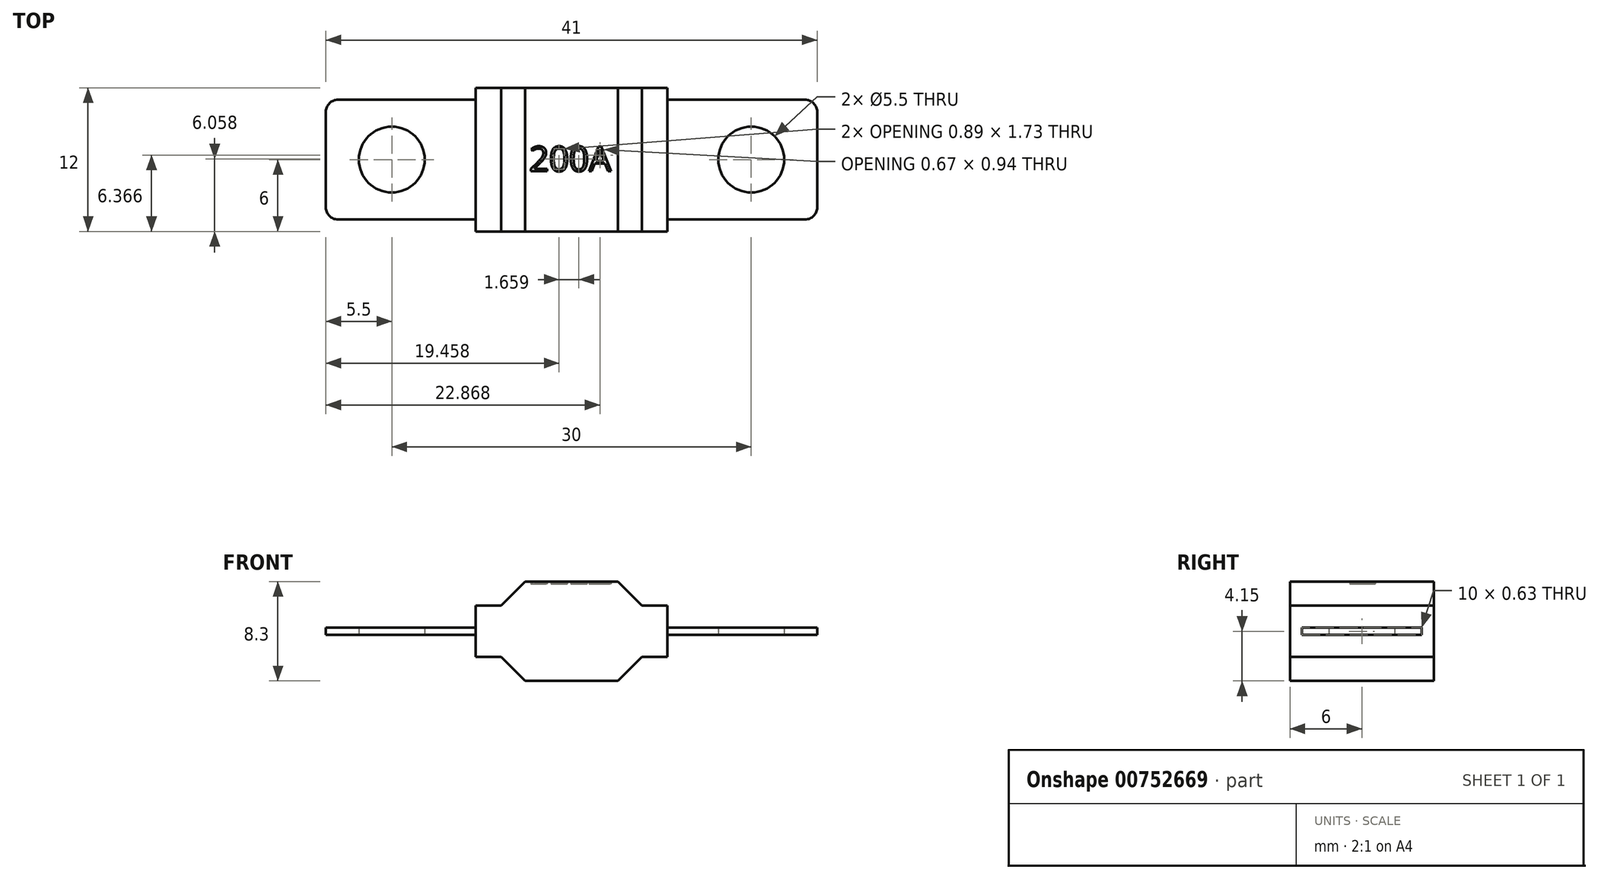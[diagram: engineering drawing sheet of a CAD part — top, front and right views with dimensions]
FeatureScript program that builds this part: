
annotation { "Feature Type Name" : "Feature", "Feature Type Description" : "" }
export const myFeature = defineFeature(function(context is Context, id is Id, definition is map)
    precondition{}
    {
        {
            var Q0;
            Q0=qCreatedBy(makeId("Top.planeOp"),FACE);
            var sketch = newSketch(context, id + "F0", { "sketchPlane" : qUnion([Q0])});
            skLineSegment(sketch, "E0.bottom", {"start": v(19.5, -5) * mm, "end": v(8, -5) * mm});
            skLineSegment(sketch, "E0.top", {"start": v(19.5, 5) * mm, "end": v(8, 5) * mm});
            skLineSegment(sketch, "E0.left", {"start": v(20.5, -4) * mm, "end": v(20.5, 4) * mm});
            skLineSegment(sketch, "E0.right", {"start": v(-20.5, -4) * mm, "end": v(-20.5, 4) * mm});
            skPoint(sketch, "E0.middle", {"position": v(0, 0) * mm});
            skLineSegment(sketch, "E1.bottom", {"start": v(8, -6) * mm, "end": v(-8, -6) * mm});
            skLineSegment(sketch, "E1.top", {"start": v(8, 6) * mm, "end": v(-8, 6) * mm});
            skLineSegment(sketch, "E1.left", {"start": v(8, -6) * mm, "end": v(8, 6) * mm});
            skLineSegment(sketch, "E1.right", {"start": v(-8, -6) * mm, "end": v(-8, 6) * mm});
            skCircle(sketch, "E2", {"center": v(-15, 0) * mm, "radius": 2.75 * mm});
            skPoint(sketch, "E2.centerSnap0", {"position": v(-20.5, 0) * mm});
            skCircle(sketch, "E3", {"center": v(15, 0) * mm, "radius": 2.75 * mm});
            skPoint(sketch, "E3.centerSnap0", {"position": v(20.5, 0) * mm});
            skLineSegment(sketch, "E4.bottom", {"start": v(15, -13.28) * mm, "end": v(-15, -13.28) * mm, "construction": true});
            skLineSegment(sketch, "E4.top", {"start": v(15, 13.28) * mm, "end": v(-15, 13.28) * mm, "construction": true});
            skLineSegment(sketch, "E4.left", {"start": v(15, -13.28) * mm, "end": v(15, 13.28) * mm, "construction": true});
            skLineSegment(sketch, "E4.right", {"start": v(-15, -13.28) * mm, "end": v(-15, 13.28) * mm, "construction": true});
            skLineSegment(sketch, "E5.trimOffspring", {"start": v(-8, 5) * mm, "end": v(-19.5, 5) * mm});
            skLineSegment(sketch, "E6.trimOffspring", {"start": v(-8, -5) * mm, "end": v(-19.5, -5) * mm});
            skPoint(sketch, "E7.visualSharp", {"position": v(-20.5, 5) * mm});
            skArc(sketch, "E7.filletArc", {"start": v(-19.5, 5) * mm, "mid": v(-20.2, 4.7) * mm, "end": v(-20.5, 4) * mm});
            skPoint(sketch, "E8.visualSharp", {"position": v(-20.5, -5) * mm});
            skArc(sketch, "E8.filletArc", {"start": v(-20.5, -4) * mm, "mid": v(-20.2, -4.7) * mm, "end": v(-19.5, -5) * mm});
            skPoint(sketch, "E9.visualSharp", {"position": v(20.5, -5) * mm});
            skArc(sketch, "E9.filletArc", {"start": v(19.5, -5) * mm, "mid": v(20.2, -4.7) * mm, "end": v(20.5, -4) * mm});
            skPoint(sketch, "E10.visualSharp", {"position": v(20.5, 5) * mm});
            skArc(sketch, "E10.filletArc", {"start": v(20.5, 4) * mm, "mid": v(20.2, 4.7) * mm, "end": v(19.5, 5) * mm});
            skSolve(sketch);
        }
        {
            var Q0;
            Q0=qSketchRegion(id+"F0",true);
            extrude(context, id + "F1", {"entities" : qUnion([Q0]), "depth" : 25 * mm, "offsetDistance" : 25 * mm});
        }
        {
            var Q0;
            Q0=makeQuery(id+"F1.opExtrude","SWEPT_FACE",FACE,{"disambiguationData":[OSD([sQuery(id+"F0.wireOp",EDGE,"E1.bottom")])]});
            var sketch = newSketch(context, id + "F2", { "sketchPlane" : qUnion([Q0])});
            skLineSegment(sketch, "E11", {"start": v(0, 25) * mm, "end": v(0, 0) * mm, "construction": true});
            skLineSegment(sketch, "E12.bottom", {"start": v(20.5, 12.19) * mm, "end": v(8, 12.19) * mm});
            skLineSegment(sketch, "E12.top", {"start": v(20.5, 12.82) * mm, "end": v(8, 12.82) * mm});
            skPoint(sketch, "E12.middle", {"position": v(0, 12.5) * mm});
            skLineSegment(sketch, "E13.bottom", {"start": v(8, 10.35) * mm, "end": v(5.86, 10.35) * mm});
            skLineSegment(sketch, "E13.top", {"start": v(8, 14.65) * mm, "end": v(5.86, 14.65) * mm});
            skLineSegment(sketch, "E13.left", {"start": v(8, 10.35) * mm, "end": v(8, 12.19) * mm});
            skLineSegment(sketch, "E13.right", {"start": v(-8, 10.35) * mm, "end": v(-8, 12.19) * mm});
            skLineSegment(sketch, "E14.bottom", {"start": v(3.86, 8.35) * mm, "end": v(-3.86, 8.35) * mm});
            skLineSegment(sketch, "E14.top", {"start": v(3.86, 16.65) * mm, "end": v(-3.86, 16.65) * mm});
            skLineSegment(sketch, "E15", {"start": v(3.86, 16.65) * mm, "end": v(5.86, 14.65) * mm});
            skLineSegment(sketch, "E16", {"start": v(-3.86, 16.65) * mm, "end": v(-5.86, 14.65) * mm});
            skLineSegment(sketch, "E17", {"start": v(-3.86, 8.35) * mm, "end": v(-5.86, 10.35) * mm});
            skLineSegment(sketch, "E18", {"start": v(3.86, 8.35) * mm, "end": v(5.86, 10.35) * mm});
            skLineSegment(sketch, "E19.trimOffspring", {"start": v(-5.86, 14.65) * mm, "end": v(-8, 14.65) * mm});
            skLineSegment(sketch, "E20.trimOffspring", {"start": v(-5.86, 10.35) * mm, "end": v(-8, 10.35) * mm});
            skLineSegment(sketch, "E21.trimOffspring", {"start": v(-8, 12.19) * mm, "end": v(-20.5, 12.19) * mm});
            skLineSegment(sketch, "E22.trimOffspring", {"start": v(-8, 12.81) * mm, "end": v(-20.5, 12.81) * mm});
            skLineSegment(sketch, "E23.trimOffspring", {"start": v(8, 12.82) * mm, "end": v(8, 14.65) * mm});
            skLineSegment(sketch, "E24.trimOffspring", {"start": v(-8, 12.81) * mm, "end": v(-8, 14.65) * mm});
            skLineSegment(sketch, "E25.bottom", {"start": v(20.85, -2.6) * mm, "end": v(-20.85, -2.6) * mm});
            skLineSegment(sketch, "E25.top", {"start": v(20.85, 27.6) * mm, "end": v(-20.85, 27.6) * mm});
            skLineSegment(sketch, "E25.left", {"start": v(20.85, -2.6) * mm, "end": v(20.85, 27.6) * mm});
            skLineSegment(sketch, "E25.right", {"start": v(-20.85, -2.6) * mm, "end": v(-20.85, 27.6) * mm});
            skPoint(sketch, "E12.left.end.orphan", {"position": v(21.22, 12.82) * mm});
            skPoint(sketch, "E26.orphan", {"position": v(21.22, 12.19) * mm});
            skPoint(sketch, "E27.orphan", {"position": v(-21.22, 12.81) * mm});
            skPoint(sketch, "E28.orphan", {"position": v(-21.22, 12.19) * mm});
            skLineSegment(sketch, "E29", {"start": v(20.5, 12.82) * mm, "end": v(20.5, 12.19) * mm});
            skLineSegment(sketch, "E30", {"start": v(-20.5, 12.81) * mm, "end": v(-20.5, 12.19) * mm});
            skSolve(sketch);
        }
        {
            var Q0;
            Q0=qSketchRegion(id+"F2",true);
            extrude(context, id + "F3", {"entities" : qUnion([Q0]), "operationType" : NewBodyOperationType.REMOVE, "oppositeDirection" : true, "depth" : 25 * mm, "offsetDistance" : 25 * mm});
        }
        {
            var Q0;
            Q0=makeQuery(id+"F3.boolean.opBoolean","COPY",FACE,{"derivedFrom":makeQuery(id+"F3.opExtrude","SWEPT_FACE",FACE,{"disambiguationData":[OSD([sQuery(id+"F2.wireOp",EDGE,"E14.top")])]})});
            var sketch = newSketch(context, id + "F4", { "sketchPlane" : qUnion([Q0])});
            skText(sketch, "E31", { "text": "200A", "fontName": "OpenSans-Regular.ttf"});
            const initialGuessF4  = {"E31": [-0.00353, -0.00098, 1, 0, 0.00209]};
            skSetInitialGuess(sketch, initialGuessF4);
            skSolve(sketch);
        }
        {
            var Q0;
            Q0=qSketchRegion(id+"F4",true);
            extrude(context, id + "F5", {"entities" : qUnion([Q0]), "operationType" : NewBodyOperationType.REMOVE, "oppositeDirection" : true, "depth" : .2 * mm, "offsetDistance" : 25 * mm});
        }
        {
            var Q0;
            Q0=makeQuery(id+"F5.boolean.opBoolean","COPY",FACE,{"derivedFrom":makeQuery(id+"F5.opExtrude","CAP_FACE",FACE,{"disambiguationData":[OSD([sQuery(id+"F4.wireOp",EDGE,"E31.sketch_text.stroke-0"),sQuery(id+"F4.wireOp",EDGE,"E31.sketch_text.stroke-1"),sQuery(id+"F4.wireOp",EDGE,"E31.sketch_text.stroke-2"),sQuery(id+"F4.wireOp",EDGE,"E31.sketch_text.stroke-3"),sQuery(id+"F4.wireOp",EDGE,"E31.sketch_text.stroke-4"),sQuery(id+"F4.wireOp",EDGE,"E31.sketch_text.stroke-5"),sQuery(id+"F4.wireOp",EDGE,"E31.sketch_text.stroke-6"),sQuery(id+"F4.wireOp",EDGE,"E31.sketch_text.stroke-7"),sQuery(id+"F4.wireOp",EDGE,"E31.sketch_text.stroke-8"),sQuery(id+"F4.wireOp",EDGE,"E31.sketch_text.stroke-9"),sQuery(id+"F4.wireOp",EDGE,"E31.sketch_text.stroke-10"),sQuery(id+"F4.wireOp",EDGE,"E31.sketch_text.stroke-11"),sQuery(id+"F4.wireOp",EDGE,"E31.sketch_text.stroke-12"),sQuery(id+"F4.wireOp",EDGE,"E31.sketch_text.stroke-13"),sQuery(id+"F4.wireOp",EDGE,"E31.sketch_text.stroke-14"),sQuery(id+"F4.wireOp",EDGE,"E31.sketch_text.stroke-15"),sQuery(id+"F4.wireOp",EDGE,"E31.sketch_text.stroke-16"),sQuery(id+"F4.wireOp",EDGE,"E31.sketch_text.stroke-17"),sQuery(id+"F4.wireOp",EDGE,"E31.sketch_text.stroke-18"),sQuery(id+"F4.wireOp",EDGE,"E31.sketch_text.stroke-19")])],"isStart":false})});
            var Q1;
            Q1=makeQuery(id+"F5.boolean.opBoolean","COPY",FACE,{"derivedFrom":makeQuery(id+"F5.opExtrude","CAP_FACE",FACE,{"disambiguationData":[OSD([sQuery(id+"F4.wireOp",EDGE,"E31.sketch_text.stroke-20"),sQuery(id+"F4.wireOp",EDGE,"E31.sketch_text.stroke-21"),sQuery(id+"F4.wireOp",EDGE,"E31.sketch_text.stroke-22"),sQuery(id+"F4.wireOp",EDGE,"E31.sketch_text.stroke-23"),sQuery(id+"F4.wireOp",EDGE,"E31.sketch_text.stroke-24"),sQuery(id+"F4.wireOp",EDGE,"E31.sketch_text.stroke-25"),sQuery(id+"F4.wireOp",EDGE,"E31.sketch_text.stroke-26"),sQuery(id+"F4.wireOp",EDGE,"E31.sketch_text.stroke-27"),sQuery(id+"F4.wireOp",EDGE,"E31.sketch_text.stroke-28"),sQuery(id+"F4.wireOp",EDGE,"E31.sketch_text.stroke-29"),sQuery(id+"F4.wireOp",EDGE,"E31.sketch_text.stroke-30"),sQuery(id+"F4.wireOp",EDGE,"E31.sketch_text.stroke-31"),sQuery(id+"F4.wireOp",EDGE,"E31.sketch_text.stroke-32"),sQuery(id+"F4.wireOp",EDGE,"E31.sketch_text.stroke-33"),sQuery(id+"F4.wireOp",EDGE,"E31.sketch_text.stroke-34"),sQuery(id+"F4.wireOp",EDGE,"E31.sketch_text.stroke-35")])],"isStart":false})});
            var Q2;
            Q2=makeQuery(id+"F5.boolean.opBoolean","COPY",FACE,{"derivedFrom":makeQuery(id+"F5.opExtrude","CAP_FACE",FACE,{"disambiguationData":[OSD([sQuery(id+"F4.wireOp",EDGE,"E31.sketch_text.stroke-36"),sQuery(id+"F4.wireOp",EDGE,"E31.sketch_text.stroke-37"),sQuery(id+"F4.wireOp",EDGE,"E31.sketch_text.stroke-38"),sQuery(id+"F4.wireOp",EDGE,"E31.sketch_text.stroke-39"),sQuery(id+"F4.wireOp",EDGE,"E31.sketch_text.stroke-40"),sQuery(id+"F4.wireOp",EDGE,"E31.sketch_text.stroke-41"),sQuery(id+"F4.wireOp",EDGE,"E31.sketch_text.stroke-42"),sQuery(id+"F4.wireOp",EDGE,"E31.sketch_text.stroke-43"),sQuery(id+"F4.wireOp",EDGE,"E31.sketch_text.stroke-44"),sQuery(id+"F4.wireOp",EDGE,"E31.sketch_text.stroke-45"),sQuery(id+"F4.wireOp",EDGE,"E31.sketch_text.stroke-46"),sQuery(id+"F4.wireOp",EDGE,"E31.sketch_text.stroke-47"),sQuery(id+"F4.wireOp",EDGE,"E31.sketch_text.stroke-48"),sQuery(id+"F4.wireOp",EDGE,"E31.sketch_text.stroke-49"),sQuery(id+"F4.wireOp",EDGE,"E31.sketch_text.stroke-50"),sQuery(id+"F4.wireOp",EDGE,"E31.sketch_text.stroke-51")])],"isStart":false})});
            var Q3;
            Q3=makeQuery(id+"F5.boolean.opBoolean","COPY",FACE,{"derivedFrom":makeQuery(id+"F5.opExtrude","CAP_FACE",FACE,{"disambiguationData":[OSD([sQuery(id+"F4.wireOp",EDGE,"E31.sketch_text.stroke-52"),sQuery(id+"F4.wireOp",EDGE,"E31.sketch_text.stroke-53"),sQuery(id+"F4.wireOp",EDGE,"E31.sketch_text.stroke-54"),sQuery(id+"F4.wireOp",EDGE,"E31.sketch_text.stroke-55"),sQuery(id+"F4.wireOp",EDGE,"E31.sketch_text.stroke-56"),sQuery(id+"F4.wireOp",EDGE,"E31.sketch_text.stroke-57"),sQuery(id+"F4.wireOp",EDGE,"E31.sketch_text.stroke-58"),sQuery(id+"F4.wireOp",EDGE,"E31.sketch_text.stroke-59"),sQuery(id+"F4.wireOp",EDGE,"E31.sketch_text.stroke-60"),sQuery(id+"F4.wireOp",EDGE,"E31.sketch_text.stroke-61"),sQuery(id+"F4.wireOp",EDGE,"E31.sketch_text.stroke-62"),sQuery(id+"F4.wireOp",EDGE,"E31.sketch_text.stroke-63"),sQuery(id+"F4.wireOp",EDGE,"E31.sketch_text.stroke-64")])],"isStart":false})});
            extrude(context, id + "F6", {"entities" : qUnion([Q0, Q1, Q2, Q3]), "depth" : .2 * mm, "offsetDistance" : 25 * mm});
        }
    });
